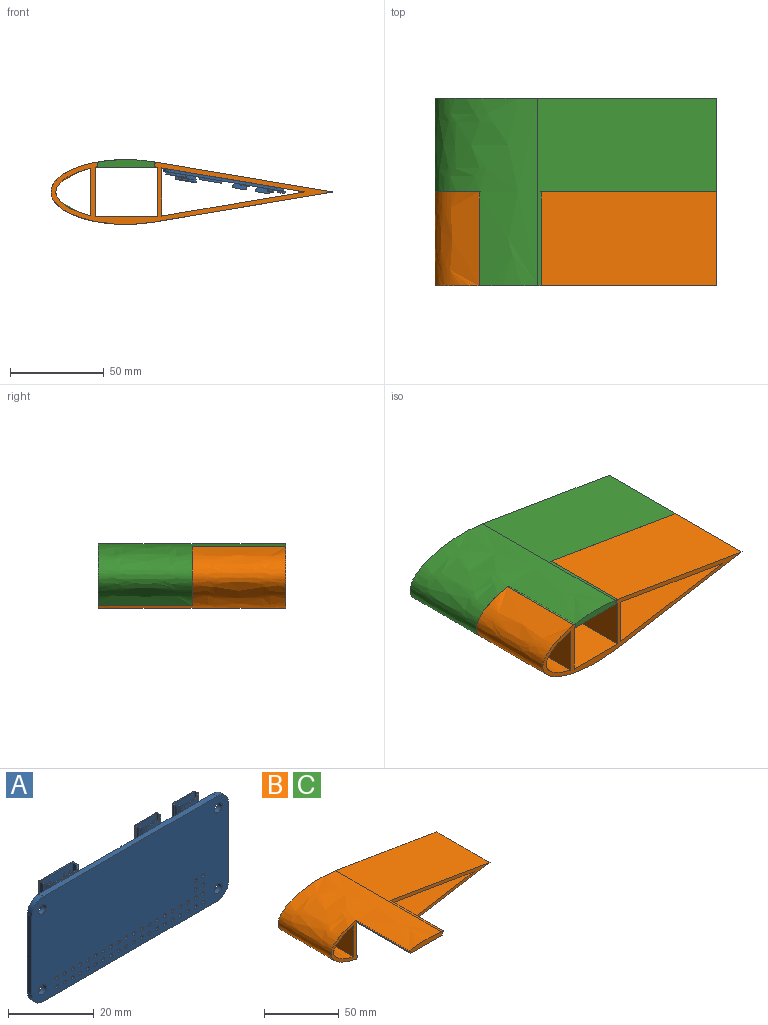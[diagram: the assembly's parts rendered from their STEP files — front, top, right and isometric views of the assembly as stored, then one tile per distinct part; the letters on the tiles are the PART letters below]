
ASSEMBLY  parts=3 mates=2
PART A: 316 faces, bbox 65.9x4.8x31.3 mm
  f0: plane 8.42x0.4mm, normal (0,-1,0), area 3.4mm2, adj f8,f9,f33,f270
  f1: plane 8.4x0.5mm, normal (0,1,0), area 4.2mm2, adj f3,f4,f5,f7
  f2: cylinder r=0.2mm len=7.6mm, axis (0,0,1), area 1.1mm2, adj f7,f10,f11,f33
  f3: plane 1.4x0.5mm, normal (-1,0,0), area 0.7mm2, adj f1,f4,f7,f13
  f4: plane 8.4x1.4mm, normal (0,0,-1), area 11.8mm2, adj f1,f3,f5,f13
  f5: plane 1.4x0.5mm, normal (1,0,0), area 0.7mm2, adj f1,f4,f7,f13
  f6: cylinder r=0.2mm len=7.6mm, axis (0,0,1), area 1.1mm2, adj f7,f15,f16,f33
  f7: plane 11.25x3.3mm, normal (0,0,-1), area 23.4mm2, adj f1,f2,f3,f5,f6,f8,f9,f10
  f8: cylinder r=0.2mm len=7.6mm, axis (0,0,1), area 1.3mm2, adj f0,f7,f16,f33,f314
  f9: cylinder r=0.2mm len=7.6mm, axis (0,0,1), area 1.3mm2, adj f0,f7,f10,f33,f314
  f10: plane 7.6x1.33mm, normal (-0.74,-0.67,0), area 13.7mm2, adj f2,f7,f9,f33
  f11: plane 7.6x1.57mm, normal (-1,0,0), area 12mm2, adj f2,f7,f12,f33
  f12: cylinder r=0.2mm len=7.6mm, axis (0,0,1), area 2.4mm2, adj f7,f11,f13,f33
  f13: plane 10.85x7.6mm, normal (0,1,0), area 72.9mm2, adj f3,f4,f5,f7,f12,f14,f17,f18
  f14: cylinder r=0.2mm len=7.6mm, axis (0,0,1), area 2.4mm2, adj f7,f13,f15,f33
  f15: plane 7.6x1.57mm, normal (1,0,0), area 12mm2, adj f6,f7,f14,f33
  f16: plane 7.6x1.33mm, normal (0.74,-0.67,0), area 13.7mm2, adj f6,f7,f8,f33
  f17: plane 0.35x0.35mm, normal (0,0,-1), area 0.1mm2, adj f13,f18,f24,f35
  f18: plane 2.95x0.35mm, normal (1,0,-0.1), area 1mm2, adj f13,f17,f19,f35
  f19: plane 1.07x0.35mm, normal (0,0,-1), area 0.4mm2, adj f13,f18,f20,f35
  f20: plane 2.95x0.35mm, normal (-1,0,-0.1), area 1mm2, adj f13,f19,f21,f35
  f21: plane 0.35x0.35mm, normal (0,0,-1), area 0.1mm2, adj f13,f20,f22,f35
  f22: plane 3.3x0.35mm, normal (1,0,0.1), area 1.2mm2, adj f13,f21,f23,f35
  f23: plane 1.7x0.35mm, normal (0,0,1), area 0.6mm2, adj f13,f22,f24,f35
  f24: plane 3.3x0.35mm, normal (-1,0,0.1), area 1.2mm2, adj f13,f17,f23,f35
  f25: plane 2.95x0.35mm, normal (1,0,-0.1), area 1mm2, adj f13,f26,f32,f35
  f26: plane 1.07x0.35mm, normal (0,0,-1), area 0.4mm2, adj f13,f25,f27,f35
  f27: plane 2.95x0.35mm, normal (-1,0,-0.1), area 1mm2, adj f13,f26,f28,f35
  f28: plane 0.35x0.35mm, normal (0,0,-1), area 0.1mm2, adj f13,f27,f29,f35
  f29: plane 3.3x0.35mm, normal (1,0,0.1), area 1.2mm2, adj f13,f28,f30,f35
  f30: plane 1.7x0.35mm, normal (0,0,1), area 0.6mm2, adj f13,f29,f31,f35
  f31: plane 3.3x0.35mm, normal (-1,0,0.1), area 1.2mm2, adj f13,f30,f32,f35
  f32: plane 0.35x0.35mm, normal (0,0,-1), area 0.1mm2, adj f13,f25,f31,f35
  f33: plane 11.25x3.3mm, normal (0,0,1), area 9.1mm2, adj f0,f2,f6,f8,f9,f10,f11,f12
  f34: plane 7x0.55mm, normal (0,0,1), area 3.8mm2, adj f41,f42,f43,f44
  f35: plane 10.55x7mm, normal (0,-1,0), area 68.5mm2, adj f17,f18,f19,f20,f21,f22,f23,f24
  f36: plane 7x1.36mm, normal (1,0,0), area 9.5mm2, adj f33,f35,f37,f45
  f37: plane 7x1.24mm, normal (0.74,0.67,0), area 11.7mm2, adj f33,f36,f38,f45
  f38: plane 8.29x7mm, normal (0,1,0), area 58mm2, adj f33,f37,f39,f45
  f39: plane 7x1.24mm, normal (-0.74,0.67,0), area 11.7mm2, adj f33,f38,f40,f45
  f40: plane 7x1.36mm, normal (-1,0,0), area 9.5mm2, adj f33,f35,f39,f45
  f41: plane 7x3.5mm, normal (0,-1,0), area 24.5mm2, adj f34,f42,f44,f45
  f42: plane 3.5x0.55mm, normal (-1,0,0), area 1.9mm2, adj f34,f41,f43,f45
  f43: plane 7x3.5mm, normal (0,1,0), area 24.5mm2, adj f34,f42,f44,f45
  f44: plane 3.5x0.55mm, normal (1,0,0), area 1.9mm2, adj f34,f41,f43,f45
  f45: plane 10.55x2.6mm, normal (0,0,1), area 22.2mm2, adj f35,f36,f37,f38,f39,f40,f41,f42
  f46: plane 3.15x0.4mm, normal (0,0,1), area 1.3mm2, adj f48,f49,f50,f51
  f47: plane 3.15x0.4mm, normal (0,0,1), area 1.3mm2, adj f52,f53,f54,f55
  f48: plane 3.5x3.15mm, normal (0,1,0), area 11mm2, adj f46,f49,f51,f61
  f49: plane 3.5x0.4mm, normal (1,0,0), area 1.4mm2, adj f46,f48,f50,f61
  f50: plane 3.5x3.15mm, normal (0,-1,0), area 11mm2, adj f46,f49,f51,f61
  f51: plane 3.5x0.4mm, normal (-1,0,0), area 1.4mm2, adj f46,f48,f50,f61
  f52: plane 3.5x3.15mm, normal (0,1,0), area 11mm2, adj f47,f53,f55,f69
  f53: plane 3.5x0.4mm, normal (1,0,0), area 1.4mm2, adj f47,f52,f54,f69
  f54: plane 3.5x3.15mm, normal (0,-1,0), area 11mm2, adj f47,f53,f55,f69
  f55: plane 3.5x0.4mm, normal (-1,0,0), area 1.4mm2, adj f47,f52,f54,f69
  f56: plane 0.32x0.23mm, normal (0,0,1), area 0.1mm2, adj f73,f74,f93,f185
  f57: plane 0.32x0.23mm, normal (0,0,1), area 0.1mm2, adj f76,f77,f93,f185
  f58: plane 0.32x0.23mm, normal (0,0,1), area 0.1mm2, adj f80,f81,f93,f185
  f59: plane 0.32x0.23mm, normal (0,0,1), area 0.1mm2, adj f78,f83,f93,f185
  f60: cylinder r=0.08mm len=5.25mm, axis (0,0,1), area 0.7mm2, adj f61,f84,f93,f193
  f61: plane 6.91x1.96mm, normal (0,0,1), area 11.2mm2, adj f48,f49,f50,f51,f60,f62,f84,f85
  f62: cylinder r=0.08mm len=5.25mm, axis (0,0,1), area 0.7mm2, adj f61,f92,f93,f193
  f63: plane 0.32x0.23mm, normal (0,0,1), area 0.1mm2, adj f94,f95,f108,f199
  f64: plane 0.32x0.23mm, normal (0,0,1), area 0.1mm2, adj f97,f98,f108,f199
  f65: plane 0.32x0.23mm, normal (0,0,1), area 0.1mm2, adj f101,f102,f108,f199
  f66: plane 0.32x0.23mm, normal (0,0,1), area 0.1mm2, adj f104,f105,f108,f199
  f67: cylinder r=0.08mm len=5.25mm, axis (0,0,1), area 0.7mm2, adj f69,f107,f108,f203
  f68: cylinder r=0.08mm len=5.25mm, axis (0,0,1), area 0.7mm2, adj f69,f108,f109,f203
  f69: plane 6.91x1.96mm, normal (0,0,1), area 11.2mm2, adj f52,f53,f54,f55,f67,f68,f106,f107
  f70: plane 1.6x0.19mm, normal (0,0,-1), area 0.3mm2, adj f183,f184,f250,f252
  f71: plane 1.6x0.19mm, normal (0,0,1), area 0.3mm2, adj f182,f184,f246,f252
  f72: plane 0.6x0.32mm, normal (0,0,1), area 0.2mm2, adj f73,f77,f93,f185
  f73: plane 0.9x0.32mm, normal (-1,0,0), area 0.3mm2, adj f56,f72,f93,f185
  f74: plane 0.45x0.32mm, normal (-1,0,0), area 0.1mm2, adj f56,f75,f93,f185
  f75: plane 1.05x0.32mm, normal (0,0,-1), area 0.3mm2, adj f74,f76,f93,f185
  f76: plane 0.45x0.32mm, normal (1,0,0), area 0.1mm2, adj f57,f75,f93,f185
  f77: plane 0.9x0.32mm, normal (1,0,0), area 0.3mm2, adj f57,f72,f93,f185
  f78: plane 0.45x0.32mm, normal (-1,0,0), area 0.1mm2, adj f59,f79,f93,f185
  f79: plane 1.05x0.32mm, normal (0,0,-1), area 0.3mm2, adj f78,f80,f93,f185
  f80: plane 0.45x0.32mm, normal (1,0,0), area 0.1mm2, adj f58,f79,f93,f185
  f81: plane 0.9x0.32mm, normal (1,0,0), area 0.3mm2, adj f58,f82,f93,f185
  f82: plane 0.6x0.32mm, normal (0,0,1), area 0.2mm2, adj f81,f83,f93,f185
  f83: plane 0.9x0.32mm, normal (-1,0,0), area 0.3mm2, adj f59,f82,f93,f185
  f84: plane 5.25x0.55mm, normal (-1,0,0), area 2.9mm2, adj f60,f61,f85,f193
  f85: cylinder r=0.68mm len=5.25mm, axis (0,0,1), area 2.7mm2, adj f61,f84,f86,f193
  f86: plane 5.25x0.65mm, normal (-0.72,0.69,0), area 4.7mm2, adj f61,f85,f87,f193
  f87: cylinder r=0.68mm len=5.25mm, axis (0,0,1), area 2.9mm2, adj f61,f86,f88,f193
  f88: plane 5.25x4.3mm, normal (0,1,0), area 22.6mm2, adj f61,f87,f89,f193
  f89: cylinder r=0.68mm len=5.25mm, axis (0,0,1), area 2.9mm2, adj f61,f88,f90,f193
  f90: plane 5.25x0.65mm, normal (0.72,0.69,0), area 4.7mm2, adj f61,f89,f91,f193
  f91: cylinder r=0.68mm len=5.25mm, axis (0,0,1), area 2.7mm2, adj f61,f90,f92,f193
  f92: plane 5.25x0.55mm, normal (1,0,0), area 2.9mm2, adj f61,f62,f91,f193
  f93: plane 6.75x5.25mm, normal (0,-1,0), area 33.4mm2, adj f56,f57,f58,f59,f60,f61,f62,f72
  f94: plane 0.9x0.32mm, normal (-1,0,0), area 0.3mm2, adj f63,f99,f108,f199
  f95: plane 0.45x0.32mm, normal (-1,0,0), area 0.1mm2, adj f63,f96,f108,f199
  f96: plane 1.05x0.32mm, normal (0,0,-1), area 0.3mm2, adj f95,f97,f108,f199
  f97: plane 0.45x0.32mm, normal (1,0,0), area 0.1mm2, adj f64,f96,f108,f199
  f98: plane 0.9x0.32mm, normal (1,0,0), area 0.3mm2, adj f64,f99,f108,f199
  f99: plane 0.6x0.32mm, normal (0,0,1), area 0.2mm2, adj f94,f98,f108,f199
  f100: plane 0.6x0.32mm, normal (0,0,1), area 0.2mm2, adj f101,f105,f108,f199
  f101: plane 0.9x0.32mm, normal (-1,0,0), area 0.3mm2, adj f65,f100,f108,f199
  f102: plane 0.45x0.32mm, normal (-1,0,0), area 0.1mm2, adj f65,f103,f108,f199
  f103: plane 1.05x0.32mm, normal (0,0,-1), area 0.3mm2, adj f102,f104,f108,f199
  f104: plane 0.45x0.32mm, normal (1,0,0), area 0.1mm2, adj f66,f103,f108,f199
  f105: plane 0.9x0.32mm, normal (1,0,0), area 0.3mm2, adj f66,f100,f108,f199
  f106: cylinder r=0.68mm len=5.25mm, axis (0,0,1), area 2.7mm2, adj f69,f107,f115,f203
  f107: plane 5.25x0.55mm, normal (-1,0,0), area 2.9mm2, adj f67,f69,f106,f203
  f108: plane 6.75x5.25mm, normal (0,-1,0), area 33.4mm2, adj f63,f64,f65,f66,f67,f68,f69,f94
  f109: plane 5.25x0.55mm, normal (1,0,0), area 2.9mm2, adj f68,f69,f110,f203
  f110: cylinder r=0.68mm len=5.25mm, axis (0,0,1), area 2.7mm2, adj f69,f109,f111,f203
  f111: plane 5.25x0.65mm, normal (0.72,0.69,0), area 4.7mm2, adj f69,f110,f112,f203
  f112: cylinder r=0.68mm len=5.25mm, axis (0,0,1), area 2.9mm2, adj f69,f111,f113,f203
  f113: plane 5.25x4.3mm, normal (0,1,0), area 22.6mm2, adj f69,f112,f114,f203
  f114: cylinder r=0.68mm len=5.25mm, axis (0,0,1), area 2.9mm2, adj f69,f113,f115,f203
  f115: plane 5.25x0.65mm, normal (-0.72,0.69,0), area 4.7mm2, adj f69,f106,f114,f203
  f116: plane 11.9x0.65mm, normal (1,0,0), area 7.7mm2, adj f117,f118,f119,f210
  f117: plane 1.4x0.65mm, normal (0,0,1), area 0.9mm2, adj f116,f118,f209,f210,f212
  f118: plane 11.9x1.4mm, normal (0,-1,0), area 16.7mm2, adj f116,f117,f119,f212
  f119: plane 1.4x0.65mm, normal (0,0,-1), area 0.9mm2, adj f116,f118,f210,f211,f212
  f120: cylinder r=1.32mm len=2.65mm, axis (0,1,0), area 11.7mm2, adj f208,f214
  f121: cylinder r=1.32mm len=2.65mm, axis (0,1,0), area 11.7mm2, adj f208,f215
  f122: cylinder r=1.32mm len=2.65mm, axis (0,1,0), area 11.7mm2, adj f208,f216
  f123: plane 0.65x0.1mm, normal (0,0,-1), area 0.1mm2, adj f124,f222,f223,f290
  f124: cylinder r=0.5mm len=0.5mm, axis (0,-1,0), area 0.1mm2, adj f123,f125,f222,f223
  f125: plane 7.75x0.1mm, normal (-1,0,0), area 0.8mm2, adj f124,f126,f222,f223
  f126: cylinder r=0.5mm len=0.5mm, axis (0,-1,0), area 0.1mm2, adj f125,f127,f222,f223
  f127: plane 0.65x0.1mm, normal (0,0,1), area 0.1mm2, adj f126,f222,f223,f282
  f128: plane 11.8x1.25mm, normal (-1,0,0), area 14.7mm2, adj f218,f221,f222,f224
  f129: sphere r=0.2mm, area 0mm2, adj f225,f226,f227
  f130: sphere r=0.2mm, area 0mm2, adj f226,f228,f229
  f131: sphere r=0.2mm, area 0mm2, adj f229,f230,f231
  f132: cylinder r=0.5mm len=1.4mm, axis (0,1,0), area 4.4mm2, adj f208,f232
  f133: cylinder r=0.5mm len=1.4mm, axis (0,1,0), area 4.4mm2, adj f208,f232
  f134: cylinder r=0.5mm len=1.4mm, axis (0,1,0), area 4.4mm2, adj f208,f232
  f135: cylinder r=0.5mm len=1.4mm, axis (0,1,0), area 4.4mm2, adj f208,f232
  f136: cylinder r=0.5mm len=1.4mm, axis (0,1,0), area 4.4mm2, adj f208,f232
  f137: cylinder r=0.5mm len=1.4mm, axis (0,1,0), area 4.4mm2, adj f208,f232
  f138: cylinder r=0.5mm len=1.4mm, axis (0,1,0), area 4.4mm2, adj f208,f232
  f139: cylinder r=0.5mm len=1.4mm, axis (0,1,0), area 4.4mm2, adj f208,f232
  f140: cylinder r=0.5mm len=1.4mm, axis (0,1,0), area 4.4mm2, adj f208,f232
  f141: cylinder r=0.5mm len=1.4mm, axis (0,1,0), area 4.4mm2, adj f208,f232
  f142: cylinder r=0.5mm len=1.4mm, axis (0,1,0), area 4.4mm2, adj f208,f232
  f143: cylinder r=0.5mm len=1.4mm, axis (0,1,0), area 4.4mm2, adj f208,f232
  f144: cylinder r=0.5mm len=1.4mm, axis (0,1,0), area 4.4mm2, adj f208,f232
  f145: cylinder r=0.5mm len=1.4mm, axis (0,1,0), area 4.4mm2, adj f208,f232
  f146: cylinder r=0.5mm len=1.4mm, axis (0,1,0), area 4.4mm2, adj f208,f232
  f147: cylinder r=0.5mm len=1.4mm, axis (0,1,0), area 4.4mm2, adj f208,f232
  f148: cylinder r=0.5mm len=1.4mm, axis (0,1,0), area 4.4mm2, adj f208,f232
  f149: cylinder r=0.5mm len=1.4mm, axis (0,1,0), area 4.4mm2, adj f208,f232
  f150: cylinder r=0.5mm len=1.4mm, axis (0,1,0), area 4.4mm2, adj f208,f232
  f151: cylinder r=0.5mm len=1.4mm, axis (0,1,0), area 4.4mm2, adj f208,f232
  f152: cylinder r=0.5mm len=1.4mm, axis (0,1,0), area 4.4mm2, adj f208,f232
  f153: cylinder r=0.5mm len=1.4mm, axis (0,1,0), area 4.4mm2, adj f208,f232
  f154: cylinder r=0.5mm len=1.4mm, axis (0,1,0), area 4.4mm2, adj f208,f232
  f155: cylinder r=0.5mm len=1.4mm, axis (0,1,0), area 4.4mm2, adj f208,f232
  f156: cylinder r=0.5mm len=1.4mm, axis (0,1,0), area 4.4mm2, adj f208,f232
  f157: cylinder r=0.5mm len=1.4mm, axis (0,1,0), area 4.4mm2, adj f208,f232
  f158: cylinder r=0.5mm len=1.4mm, axis (0,1,0), area 4.4mm2, adj f208,f232
  f159: cylinder r=0.5mm len=1.4mm, axis (0,1,0), area 4.4mm2, adj f208,f232
  f160: cylinder r=0.5mm len=1.4mm, axis (0,1,0), area 4.4mm2, adj f208,f232
  f161: cylinder r=0.5mm len=1.4mm, axis (0,1,0), area 4.4mm2, adj f208,f232
  f162: cylinder r=0.5mm len=1.4mm, axis (0,1,0), area 4.4mm2, adj f208,f232
  f163: cylinder r=0.5mm len=1.4mm, axis (0,1,0), area 4.4mm2, adj f208,f232
  f164: cylinder r=0.5mm len=1.4mm, axis (0,1,0), area 4.4mm2, adj f208,f232
  f165: cylinder r=0.5mm len=1.4mm, axis (0,1,0), area 4.4mm2, adj f208,f232
  f166: cylinder r=0.5mm len=1.4mm, axis (0,1,0), area 4.4mm2, adj f208,f232
  f167: cylinder r=0.5mm len=1.4mm, axis (0,1,0), area 4.4mm2, adj f208,f232
  f168: cylinder r=0.5mm len=1.4mm, axis (0,1,0), area 4.4mm2, adj f208,f232
  f169: cylinder r=0.5mm len=1.4mm, axis (0,1,0), area 4.4mm2, adj f208,f232
  f170: cylinder r=0.5mm len=1.4mm, axis (0,1,0), area 4.4mm2, adj f208,f232
  f171: cylinder r=0.5mm len=1.4mm, axis (0,1,0), area 4.4mm2, adj f208,f232
  f172: cylinder r=0.5mm len=1.4mm, axis (0,1,0), area 4.4mm2, adj f208,f232
  f173: cylinder r=0.5mm len=1.4mm, axis (0,1,0), area 4.4mm2, adj f208,f232
  f174: cylinder r=0.5mm len=1.4mm, axis (0,1,0), area 4.4mm2, adj f208,f232
  f175: cylinder r=0.5mm len=1.4mm, axis (0,1,0), area 4.4mm2, adj f208,f232
  f176: sphere r=0.2mm, area 0mm2, adj f231,f233,f235
  f177: sphere r=0.2mm, area 0mm2, adj f235,f236,f237
  f178: sphere r=0.2mm, area 0mm2, adj f236,f238,f239
  f179: plane 3.6x3.25mm, normal (0,1,0), area 10.5mm2, adj f225,f226,f229,f231,f235,f236,f238,f241
  f180: sphere r=0.2mm, area 0mm2, adj f238,f241,f242
  f181: sphere r=0.2mm, area 0mm2, adj f225,f240,f241
  f182: plane 1.7x1.6mm, normal (0,1,0), area 2.7mm2, adj f71,f245,f246,f252
  f183: plane 1.7x1.6mm, normal (0,1,0), area 2.7mm2, adj f70,f250,f251,f252
  f184: plane 16x2.7mm, normal (0,1,0), area 36.8mm2, adj f70,f71,f246,f247,f248,f249,f250,f252
  f185: plane 6.75x5.75mm, normal (0,1,0), area 36.8mm2, adj f56,f57,f58,f59,f72,f73,f74,f75
  f186: cylinder r=0.4mm len=5.75mm, axis (0,0,1), area 3.6mm2, adj f185,f187,f193,f265
  f187: plane 5.75x0.55mm, normal (-1,0,0), area 3.1mm2, adj f186,f188,f193,f265
  f188: cylinder r=1mm len=5.75mm, axis (0,0,1), area 4.4mm2, adj f187,f189,f193,f265
  f189: plane 5.75x0.65mm, normal (-0.72,-0.69,0), area 5.2mm2, adj f188,f193,f264,f265
  f190: cylinder r=1mm len=5.75mm, axis (0,0,1), area 4.4mm2, adj f191,f193,f194,f265
  f191: plane 5.75x0.55mm, normal (1,0,0), area 3.1mm2, adj f190,f192,f193,f265
  f192: cylinder r=0.4mm len=5.75mm, axis (0,0,1), area 3.6mm2, adj f185,f191,f193,f265
  f193: plane 7.55x2.6mm, normal (0,0,1), area 5.6mm2, adj f60,f62,f84,f85,f86,f87,f88,f89
  f194: plane 5.75x0.65mm, normal (0.72,-0.69,0), area 5.2mm2, adj f190,f193,f265,f266
  f195: plane 5.75x0.65mm, normal (-0.72,-0.69,0), area 5.2mm2, adj f196,f203,f267,f268
  f196: cylinder r=1mm len=5.75mm, axis (0,0,1), area 4.4mm2, adj f195,f197,f203,f268
  f197: plane 5.75x0.55mm, normal (-1,0,0), area 3.1mm2, adj f196,f198,f203,f268
  f198: cylinder r=0.4mm len=5.75mm, axis (0,0,1), area 3.6mm2, adj f197,f199,f203,f268
  f199: plane 6.75x5.75mm, normal (0,1,0), area 36.8mm2, adj f63,f64,f65,f66,f94,f95,f96,f97
  f200: cylinder r=0.4mm len=5.75mm, axis (0,0,1), area 3.6mm2, adj f199,f201,f203,f268
  f201: plane 5.75x0.55mm, normal (1,0,0), area 3.1mm2, adj f200,f202,f203,f268
  f202: cylinder r=1mm len=5.75mm, axis (0,0,1), area 4.4mm2, adj f201,f203,f204,f268
  f203: plane 7.55x2.6mm, normal (0,0,1), area 5.6mm2, adj f67,f68,f106,f107,f108,f109,f110,f111
  f204: plane 5.75x0.65mm, normal (0.72,-0.69,0), area 5.2mm2, adj f202,f203,f268,f269
  f205: plane 4.3x1.25mm, normal (0,-1,0), area 5.4mm2, adj f193,f264,f266,f270
  f206: plane 4.3x1.25mm, normal (0,-1,0), area 5.4mm2, adj f203,f267,f269,f270
  f207: plane 8x3.45mm, normal (0,1,0), area 14.5mm2, adj f259,f260,f261,f262,f263,f270
  f208: plane 65x30mm, normal (0,-1,0), area 1881.3mm2, adj f120,f121,f122,f132,f133,f134,f135,f136
  f209: plane 2.55x0.9mm, normal (0,-1,0), area 2.3mm2, adj f117,f212,f253,f272
  f210: plane 11.9x0.5mm, normal (0,1,0), area 6mm2, adj f116,f117,f119,f272
  f211: plane 2.55x0.9mm, normal (0,-1,0), area 2.3mm2, adj f119,f212,f272,f273
  f212: plane 17x1.2mm, normal (1,0,0), area 12.7mm2, adj f117,f118,f119,f209,f211,f213,f253,f273
  f213: plane 17x1.4mm, normal (0,1,0), area 23.8mm2, adj f212,f252,f253,f273
  f214: plane 6x6mm, normal (0,1,0), area 22.8mm2, adj f120,f274
  f215: plane 6x6mm, normal (0,1,0), area 22.8mm2, adj f121,f275
  f216: plane 6x6mm, normal (0,1,0), area 22.8mm2, adj f122,f276
  f217: plane 12x12mm, normal (0,1,0), area 144mm2, adj f277,f278,f279,f280
  f218: plane 10.65x1.25mm, normal (0,0,1), area 13.3mm2, adj f128,f222,f224,f282
  f219: cylinder r=0.1mm len=11.4mm, axis (-1,0,0), area 1.8mm2, adj f223,f282,f283,f284
  f220: cylinder r=0.1mm len=11.4mm, axis (1,0,0), area 1.8mm2, adj f223,f288,f289,f290
  f221: plane 10.65x1.25mm, normal (0,0,-1), area 13.3mm2, adj f128,f222,f224,f290
  f222: plane 11.8x10.65mm, normal (0,-1,0), area 115.7mm2, adj f123,f124,f125,f126,f127,f128,f218,f221
  f223: plane 11.8x11.4mm, normal (0,1,0), area 122.5mm2, adj f123,f124,f125,f126,f127,f219,f220,f282
  f224: plane 11.8x10.65mm, normal (0,1,0), area 115.7mm2, adj f128,f218,f221,f281,f282,f290,f291,f292
  f225: cylinder r=0.2mm len=1.68mm, axis (-1,0,0), area 0.5mm2, adj f129,f179,f181,f295
  f226: cylinder r=0.2mm len=0.92mm, axis (-0.71,0,-0.71), area 0.3mm2, adj f129,f130,f179,f296
  f227: cylinder r=0.2mm len=1.3mm, axis (0,-1,0), area 0.2mm2, adj f129,f295,f296,f314
  f228: cylinder r=0.2mm len=1.3mm, axis (0,1,0), area 0.2mm2, adj f130,f296,f297,f314
  f229: cylinder r=0.2mm len=2.03mm, axis (0,0,-1), area 0.6mm2, adj f130,f131,f179,f297
  f230: cylinder r=0.2mm len=1.3mm, axis (0,-1,0), area 0.2mm2, adj f131,f297,f298,f314
  f231: cylinder r=0.2mm len=0.92mm, axis (0.71,0,-0.71), area 0.3mm2, adj f131,f176,f179,f298
  f232: plane 51x10.1mm, normal (0,1,0), area 251mm2, adj f132,f133,f134,f135,f136,f137,f138,f139
  f233: cylinder r=0.2mm len=1.3mm, axis (0,1,0), area 0.2mm2, adj f176,f234,f298,f305,f314
  f234: plane 0.8x0.05mm, normal (0,-1,0), area 0mm2, adj f233,f299,f304,f305
  f235: cylinder r=0.2mm len=1.68mm, axis (1,0,0), area 0.5mm2, adj f176,f177,f179,f305
  f236: cylinder r=0.2mm len=0.92mm, axis (0.71,0,0.71), area 0.3mm2, adj f177,f178,f179,f306
  f237: cylinder r=0.2mm len=1.3mm, axis (0,-1,0), area 0.2mm2, adj f177,f305,f306,f314
  f238: cylinder r=0.2mm len=2.03mm, axis (0,0,1), area 0.6mm2, adj f178,f179,f180,f307
  f239: cylinder r=0.2mm len=1.3mm, axis (0,1,0), area 0.2mm2, adj f178,f306,f307,f314
  f240: cylinder r=0.2mm len=1.3mm, axis (0,1,0), area 0.2mm2, adj f181,f295,f308,f314
  f241: cylinder r=0.2mm len=0.92mm, axis (-0.71,0,0.71), area 0.3mm2, adj f179,f180,f181,f308
  f242: cylinder r=0.2mm len=1.3mm, axis (0,-1,0), area 0.2mm2, adj f180,f307,f308,f314
  f243: plane 5x3.15mm, normal (0,1,0), area 15.8mm2, adj f309,f310,f311,f312
  f244: cylinder r=1.32mm len=2.65mm, axis (0,1,0), area 11.7mm2, adj f208,f313
  f245: plane 1.6x1mm, normal (0,0,1), area 1.6mm2, adj f182,f246,f252,f314
  f246: plane 2x1.19mm, normal (1,0,0), area 0.7mm2, adj f71,f182,f184,f245,f247,f314
  f247: plane 1.19x1.1mm, normal (0,0,1), area 1.3mm2, adj f184,f246,f248,f314
  f248: plane 16x1.19mm, normal (-1,0,0), area 19mm2, adj f184,f247,f249,f314
  f249: plane 1.19x1.1mm, normal (0,0,-1), area 1.3mm2, adj f184,f248,f250,f314
  f250: plane 2x1.19mm, normal (1,0,0), area 0.7mm2, adj f70,f183,f184,f249,f251,f314
  f251: plane 1.6x1mm, normal (0,0,-1), area 1.6mm2, adj f183,f250,f252,f314
  f252: plane 17x1.2mm, normal (-1,0,0), area 2.7mm2, adj f70,f71,f182,f183,f184,f213,f245,f251
  f253: plane 1.4x1.2mm, normal (0,0,-1), area 1.7mm2, adj f209,f212,f213,f252,f314
  f254: cylinder r=3.75mm len=3.75mm, axis (0,-1,0), area 8.8mm2, adj f208,f255,f272,f314
  f255: plane 57.5x1.5mm, normal (0,0,-1), area 86.2mm2, adj f208,f254,f256,f314
  f256: cylinder r=3.75mm len=3.75mm, axis (0,-1,0), area 8.8mm2, adj f208,f255,f257,f314
  f257: plane 22.5x1.5mm, normal (-1,0,0), area 33.8mm2, adj f208,f256,f258,f314
  f258: cylinder r=3.75mm len=3.75mm, axis (0,-1,0), area 8.8mm2, adj f208,f257,f270,f314
  f259: plane 0.8x0.1mm, normal (1,0,0), area 0.1mm2, adj f207,f260,f270,f314
  f260: plane 3.08x2.65mm, normal (0.65,0,-0.76), area 0.4mm2, adj f207,f259,f261,f314
  f261: plane 8x0.1mm, normal (0,0,1), area 0.8mm2, adj f207,f260,f262,f314
  f262: plane 3.08x2.65mm, normal (-0.65,0,-0.76), area 0.4mm2, adj f207,f261,f263,f314
  f263: plane 0.8x0.1mm, normal (-1,0,0), area 0.1mm2, adj f207,f262,f270,f314
  f264: cylinder r=1mm len=5.75mm, axis (0,0,1), area 4.6mm2, adj f189,f193,f205,f265,f314
  f265: plane 7.55x2.6mm, normal (0,0,-1), area 18mm2, adj f185,f186,f187,f188,f189,f190,f191,f192
  f266: cylinder r=1mm len=5.75mm, axis (0,0,1), area 4.6mm2, adj f193,f194,f205,f265,f314
  f267: cylinder r=1mm len=5.75mm, axis (0,0,1), area 4.6mm2, adj f195,f203,f206,f268,f314
  f268: plane 7.55x2.6mm, normal (0,0,-1), area 18mm2, adj f195,f196,f197,f198,f199,f200,f201,f202
  f269: cylinder r=1mm len=5.75mm, axis (0,0,1), area 4.6mm2, adj f203,f204,f206,f268,f314
  f270: plane 57.5x1.5mm, normal (0,0,1), area 86.1mm2, adj f0,f205,f206,f207,f208,f258,f259,f263
  f271: cylinder r=3.75mm len=3.75mm, axis (0,-1,0), area 8.8mm2, adj f208,f270,f272,f314
  f272: plane 22.5x1.5mm, normal (1,0,0), area 33.8mm2, adj f208,f209,f210,f211,f254,f271,f314
  f273: plane 1.4x1.2mm, normal (0,0,1), area 1.7mm2, adj f211,f212,f213,f252,f314
  f274: cylinder r=3mm len=6mm, axis (0,1,0), area 1.9mm2, adj f214,f314
  f275: cylinder r=3mm len=6mm, axis (0,1,0), area 1.9mm2, adj f215,f314
  f276: cylinder r=3mm len=6mm, axis (0,1,0), area 1.9mm2, adj f216,f314
  f277: plane 12x1.25mm, normal (0,0,-1), area 15mm2, adj f217,f278,f280,f314
  f278: plane 12x1.25mm, normal (1,0,0), area 15mm2, adj f217,f277,f279,f314
  f279: plane 12x1.25mm, normal (0,0,1), area 15mm2, adj f217,f278,f280,f314
  f280: plane 12x1.25mm, normal (-1,0,0), area 15mm2, adj f217,f277,f279,f314
  f281: plane 0.65x0.1mm, normal (0,0,1), area 0.1mm2, adj f224,f282,f294,f314
  f282: plane 1.45x1.1mm, normal (-1,0,0), area 0.3mm2, adj f127,f218,f219,f222,f223,f224,f281,f283
  f283: plane 11.4x1.35mm, normal (0,0,-1), area 15.4mm2, adj f219,f282,f284,f314
  f284: plane 1.45x1.1mm, normal (1,0,0), area 1.6mm2, adj f219,f223,f283,f285,f314
  f285: plane 1.45x0.25mm, normal (0.71,0,0.71), area 0.5mm2, adj f223,f284,f286,f314
  f286: plane 7.9x1.45mm, normal (1,0,0), area 11.5mm2, adj f223,f285,f287,f314
  f287: plane 1.45x0.25mm, normal (0.71,0,-0.71), area 0.5mm2, adj f223,f286,f288,f314
  f288: plane 2.5x1.45mm, normal (1,0,0), area 3.6mm2, adj f220,f223,f287,f289,f314
  f289: plane 11.4x1.35mm, normal (0,0,1), area 15.4mm2, adj f220,f288,f290,f314
  f290: plane 2.15x1.45mm, normal (-1,0,0), area 0.6mm2, adj f123,f220,f221,f222,f223,f224,f289,f291
  f291: plane 0.65x0.1mm, normal (0,0,-1), area 0.1mm2, adj f224,f290,f292,f314
  f292: cylinder r=0.5mm len=0.5mm, axis (0,-1,0), area 0.1mm2, adj f224,f291,f293,f314
  f293: plane 7.75x0.1mm, normal (-1,0,0), area 0.8mm2, adj f224,f292,f294,f314
  f294: cylinder r=0.5mm len=0.5mm, axis (0,-1,0), area 0.1mm2, adj f224,f281,f293,f314
  f295: plane 1.68x1.3mm, normal (0,0,1), area 2.2mm2, adj f225,f227,f240,f314
  f296: plane 1.3x0.78mm, normal (-0.71,0,0.71), area 1.4mm2, adj f226,f227,f228,f314
  f297: plane 2.03x1.3mm, normal (-1,0,0), area 2.6mm2, adj f228,f229,f230,f314
  f298: plane 1.3x0.78mm, normal (-0.71,0,-0.71), area 1.4mm2, adj f230,f231,f233,f314
  f299: plane 5.1x0.1mm, normal (0,0,-1), area 0.5mm2, adj f232,f234,f300,f304,f314
  f300: plane 5x0.1mm, normal (1,0,0), area 0.5mm2, adj f232,f299,f301,f314
  f301: plane 45.9x0.1mm, normal (0,0,-1), area 4.6mm2, adj f232,f300,f302,f314
  f302: plane 5.1x0.1mm, normal (1,0,0), area 0.5mm2, adj f232,f301,f303,f314
  f303: plane 51x0.1mm, normal (0,0,1), area 5.1mm2, adj f232,f302,f304,f314
  f304: plane 10.1x0.1mm, normal (-1,0,0), area 1mm2, adj f232,f234,f299,f303,f314
  f305: plane 1.68x1.3mm, normal (0,0,-1), area 2.2mm2, adj f233,f234,f235,f237,f314
  f306: plane 1.3x0.78mm, normal (0.71,0,-0.71), area 1.4mm2, adj f236,f237,f239,f314
  f307: plane 2.03x1.3mm, normal (1,0,0), area 2.6mm2, adj f238,f239,f242,f314
  f308: plane 1.3x0.78mm, normal (0.71,0,0.71), area 1.4mm2, adj f240,f241,f242,f314
  f309: plane 5x0.5mm, normal (0,0,1), area 2.5mm2, adj f243,f310,f312,f314
  f310: plane 3.15x0.5mm, normal (-1,0,0), area 1.6mm2, adj f243,f309,f311,f314
  f311: plane 5x0.5mm, normal (0,0,-1), area 2.5mm2, adj f243,f310,f312,f314
  f312: plane 3.15x0.5mm, normal (1,0,0), area 1.6mm2, adj f243,f309,f311,f314
  f313: plane 6x6mm, normal (0,1,0), area 22.8mm2, adj f244,f315
  f314: plane 65x30mm, normal (0,1,0), area 1077.1mm2, adj f7,f8,f9,f227,f228,f230,f233,f237
  f315: cylinder r=3mm len=6mm, axis (0,1,0), area 1.9mm2, adj f313,f314
PART B: 21 faces, bbox 150x100x33 mm
  f0: plane 100x32.75mm, normal (0,0,-1), area 3148.1mm2, adj f1,f3,f4,f5,f9,f10,f19,f20
  f1: plane 33.21x4.06mm, normal (0,-1,0), area 111mm2, adj f0,f2,f6,f7,f18,f19,f20
  f2: cylinder r=1.28mm len=50mm, axis (0,1,0), area 110.9mm2, adj f1,f4,f6,f19
  f3: plane 31.45x24.89mm, normal (0,-1,0), area 211.6mm2, adj f0,f7,f9,f11,f12,f17,f18,f20
  f4: plane 94.9x31.51mm, normal (0,-1,0), area 507.2mm2, adj f0,f2,f6,f8,f10,f13,f14,f15
  f5: plane 150x33.01mm, normal (0,1,0), area 829.8mm2, adj f0,f6,f7,f8,f9,f10,f11,f12
  f6: plane 100x95.45mm, normal (0.17,0,0.99), area 4943.5mm2, adj f1,f2,f4,f5,f7,f8
  f7: extruded ~100x54.54mm, area 6137.4mm2, adj f1,f3,f5,f6,f17,f18
  f8: plane 93.41x50mm, normal (0.17,0,-0.99), area 4736.4mm2, adj f4,f5,f6,f16
  f9: plane 50x26.4mm, normal (1,0,0), area 1320mm2, adj f0,f3,f5,f17
  f10: plane 50x26.4mm, normal (-1,0,0), area 1320mm2, adj f0,f4,f5,f16
  f11: plane 50x25.3mm, normal (-1,0,0), area 1265mm2, adj f3,f5,f12
  f12: extruded ~50x25.3mm, area 2379.6mm2, adj f3,f5,f11
  f13: plane 76.07x50mm, normal (-0.17,0,-0.99), area 3857.3mm2, adj f4,f5,f14,f15
  f14: plane 50x25.63mm, normal (1,0,0), area 1281.5mm2, adj f4,f5,f13,f15
  f15: plane 76.07x50mm, normal (-0.17,0,0.99), area 3857.3mm2, adj f4,f5,f13,f14
  f16: cylinder r=1.28mm len=50mm, axis (0,-1,0), area 211.2mm2, adj f4,f5,f8,f10
  f17: cylinder r=1.26mm len=50mm, axis (0,-1,0), area 210.5mm2, adj f3,f5,f7,f9
  f18: cylinder r=1.26mm len=50mm, axis (0,1,0), area 111.4mm2, adj f1,f3,f7,f20
  f19: plane 50x1.28mm, normal (1,0,0), area 63.8mm2, adj f0,f1,f2,f4
  f20: plane 50x1.26mm, normal (-1,0,0), area 63.1mm2, adj f0,f1,f3,f18
PART C: same geometry as B
PLACE A rot(axis=(-0.99,0.08,0.08),90.4deg) t=(51.99,23.99,-5.96)mm
PLACE B rot(axis=(1,0,0),180deg) t=(0,-26.01,-13.18)mm
PLACE C t=(0,23.99,-13.2)mm
MATE fastened A.f208 <-> C.f13  axis (0.17,0,0.99) through (51.99,23.99,-5.96)mm
MATE fastened C.f4 <-> B.f4  axis (0,-1,0) through (53.68,-1.01,-13.19)mm
